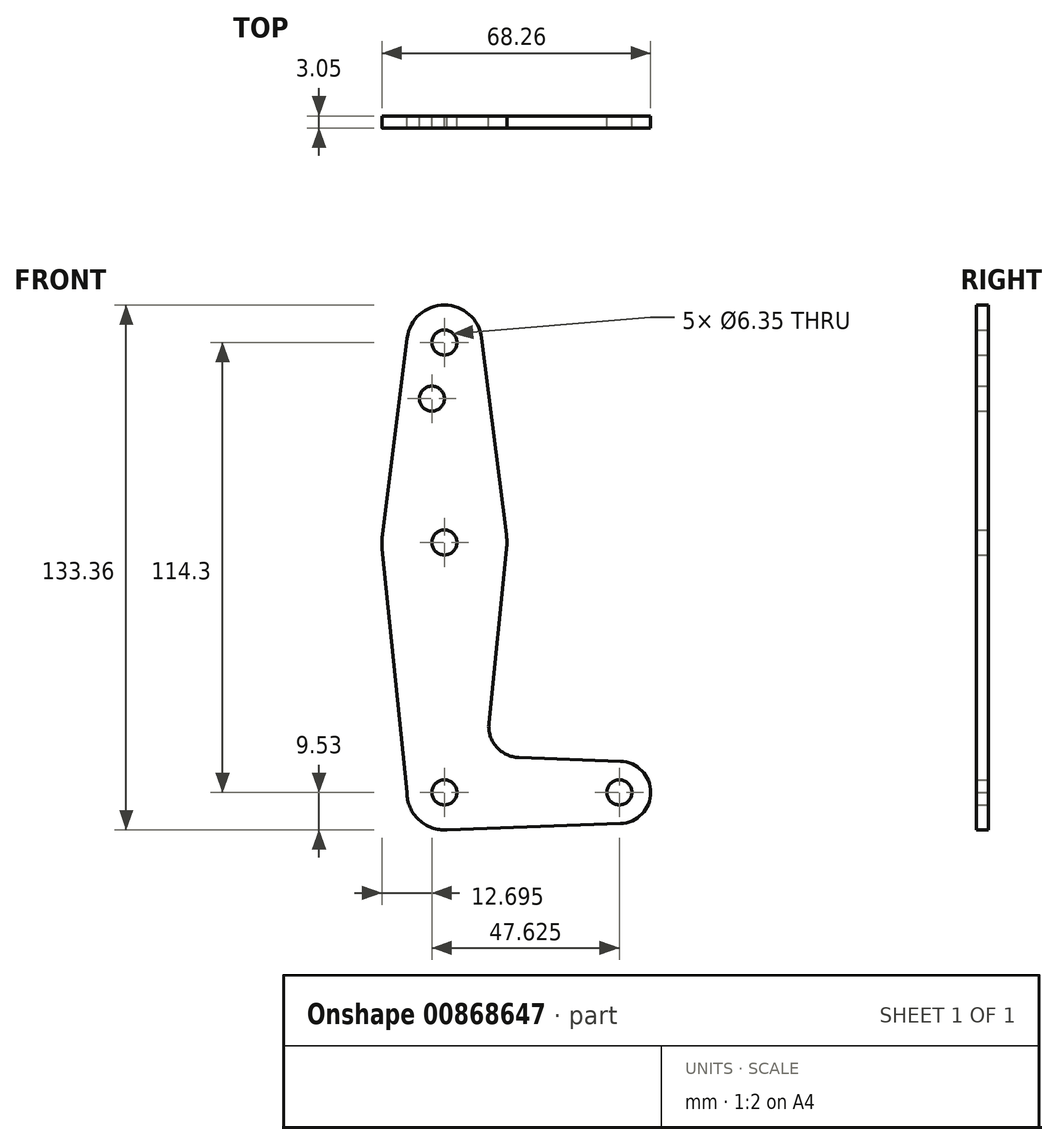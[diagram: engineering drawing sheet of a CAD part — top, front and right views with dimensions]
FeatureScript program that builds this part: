
annotation { "Feature Type Name" : "Feature", "Feature Type Description" : "" }
export const myFeature = defineFeature(function(context is Context, id is Id, definition is map)
    precondition{}
    {
        {
            var Q0;
            Q0=qCreatedBy(makeId("Front.planeOp"),FACE);
            var sketch = newSketch(context, id + "F0", { "sketchPlane" : qUnion([Q0])});
            skLineSegment(sketch, "E0", {"start": v(0, 0) * mm, "end": v(0, 114.3) * mm, "construction": true});
            skLineSegment(sketch, "E1", {"start": v(0, 0) * mm, "end": v(44.45, 0) * mm, "construction": true});
            skCircle(sketch, "E2", {"center": v(0, 114.3) * mm, "radius": 9.53 * mm});
            skCircle(sketch, "E3", {"center": v(0, 0) * mm, "radius": 9.53 * mm});
            skCircle(sketch, "E4", {"center": v(0, 63.5) * mm, "radius": 15.88 * mm});
            skCircle(sketch, "E5", {"center": v(44.45, 0) * mm, "radius": 7.94 * mm});
            skLineSegment(sketch, "E6", {"start": v(9.45, 115.5) * mm, "end": v(15.75, 65.48) * mm});
            skLineSegment(sketch, "E7", {"start": v(-9.45, 115.5) * mm, "end": v(-15.75, 65.48) * mm});
            skLineSegment(sketch, "E8", {"start": v(-9.52, 0) * mm, "end": v(-15.8, 61.9) * mm});
            skLineSegment(sketch, "E9", {"start": v(11.3, 17.6) * mm, "end": v(15.8, 61.9) * mm});
            skLineSegment(sketch, "E10", {"start": v(18.93, 8.85) * mm, "end": v(44.73, 7.93) * mm});
            skLineSegment(sketch, "E11", {"start": v(0, -9.53) * mm, "end": v(44.73, -7.93) * mm});
            skCircle(sketch, "E12", {"center": v(0, 114.3) * mm, "radius": 3.18 * mm});
            skCircle(sketch, "E13", {"center": v(-3.18, 100.03) * mm, "radius": 3.18 * mm});
            skCircle(sketch, "E14", {"center": v(0, 63.5) * mm, "radius": 3.17 * mm});
            skCircle(sketch, "E15", {"center": v(0, 0) * mm, "radius": 3.17 * mm});
            skCircle(sketch, "E16", {"center": v(44.45, 0) * mm, "radius": 3.18 * mm});
            skArc(sketch, "E17.filletArc", {"start": v(11.3, 17.6) * mm, "mid": v(13.22, 11.57) * mm, "end": v(18.93, 8.85) * mm});
            skSolve(sketch);
        }
        {
            var Q0;
            Q0 = qSketchRegion(id + "F0", true);
            extrude(context, id + "F1", {"entities" : qUnion([Q0]), "depth" : 3.05 * mm, "offsetDistance" : 25.4 * mm});
        }
    });
